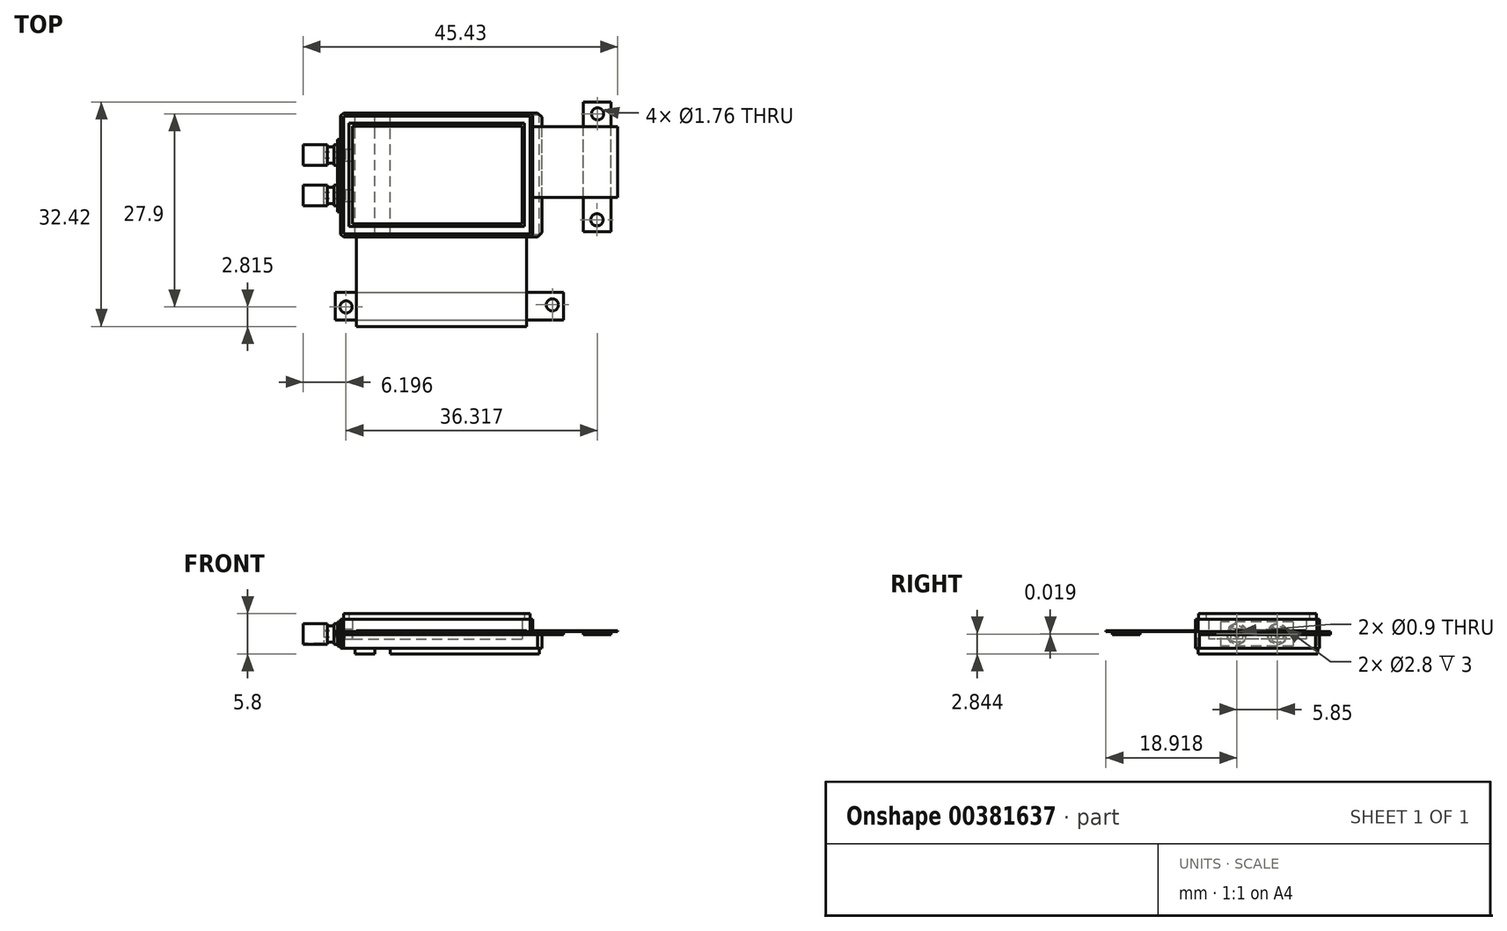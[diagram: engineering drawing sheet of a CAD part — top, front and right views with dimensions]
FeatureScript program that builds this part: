
annotation { "Feature Type Name" : "Feature", "Feature Type Description" : "" }
export const myFeature = defineFeature(function(context is Context, id is Id, definition is map)
    precondition{}
    {
        {
            var Q0;
            Q0=qCreatedBy(makeId("Top.planeOp"),FACE);
            var sketch = newSketch(context, id + "F0", { "sketchPlane" : qUnion([Q0])});
            skLineSegment(sketch, "E0.bottom", {"start": v(-8, 13.05) * mm, "end": v(19.71, 13.05) * mm});
            skLineSegment(sketch, "E0.top", {"start": v(-8, -4.87) * mm, "end": v(19.71, -4.87) * mm});
            skLineSegment(sketch, "E0.left", {"start": v(-8, 13.05) * mm, "end": v(-8, -4.87) * mm});
            skLineSegment(sketch, "E0.right", {"start": v(19.71, 13.05) * mm, "end": v(19.71, -4.87) * mm});
            skLineSegment(sketch, "E1.bottom", {"start": v(-6.33, 11.15) * mm, "end": v(18.21, 11.15) * mm});
            skLineSegment(sketch, "E1.top", {"start": v(-6.33, -2.97) * mm, "end": v(18.21, -2.97) * mm});
            skLineSegment(sketch, "E1.left", {"start": v(-6.33, 11.15) * mm, "end": v(-6.33, -2.97) * mm});
            skLineSegment(sketch, "E1.right", {"start": v(18.21, 11.15) * mm, "end": v(18.21, -2.97) * mm});
            skSolve(sketch);
        }
        {
            var Q0;
            Q0=makeQuery(id+"F0.imprint","IMPRINT",FACE,{"disambiguationData":[TD([[makeQuery(id+"F0.imprint","IMPRINT",EDGE,{"derivedFrom":sQuery(id+"F0.wireOp",EDGE,"E0.bottom")}),-1.0]])]});
            extrude(context, id + "F1", {"entities" : qUnion([Q0]), "depth" : 1.78 * mm});
        }
        {
            var Q0;
            Q0=makeQuery(id+"F1.opExtrude","CAP_FACE",FACE,{"disambiguationData":[OSD([sQuery(id+"F0.wireOp",EDGE,"E0.bottom"),sQuery(id+"F0.wireOp",EDGE,"E0.top"),sQuery(id+"F0.wireOp",EDGE,"E0.left"),sQuery(id+"F0.wireOp",EDGE,"E0.right"),sQuery(id+"F0.wireOp",EDGE,"E1.bottom"),sQuery(id+"F0.wireOp",EDGE,"E1.top"),sQuery(id+"F0.wireOp",EDGE,"E1.left"),sQuery(id+"F0.wireOp",EDGE,"E1.right")])],"isStart":false});
            var sketch = newSketch(context, id + "F2", { "sketchPlane" : qUnion([Q0])});
            skLineSegment(sketch, "E2.bottom", {"start": v(-7.6, 12.6) * mm, "end": v(19.32, 12.6) * mm});
            skLineSegment(sketch, "E2.top", {"start": v(-7.6, -4.41) * mm, "end": v(19.32, -4.41) * mm});
            skLineSegment(sketch, "E2.left", {"start": v(-7.6, 12.6) * mm, "end": v(-7.6, -4.41) * mm});
            skLineSegment(sketch, "E2.right", {"start": v(19.32, 12.6) * mm, "end": v(19.32, -4.41) * mm});
            skLineSegment(sketch, "E3.bottom", {"start": v(-6.79, 11.56) * mm, "end": v(18.51, 11.56) * mm});
            skLineSegment(sketch, "E3.top", {"start": v(-6.79, -3.34) * mm, "end": v(18.51, -3.34) * mm});
            skLineSegment(sketch, "E3.left", {"start": v(-6.79, 11.56) * mm, "end": v(-6.79, -3.34) * mm});
            skLineSegment(sketch, "E3.right", {"start": v(18.51, 11.56) * mm, "end": v(18.51, -3.34) * mm});
            skSolve(sketch);
        }
        {
            var Q0;
            Q0=makeQuery(id+"F2.imprint","IMPRINT",FACE,{"disambiguationData":[TD([[makeQuery(id+"F2.imprint","IMPRINT",EDGE,{"derivedFrom":sQuery(id+"F2.wireOp",EDGE,"E2.bottom")}),-1.0]])]});
            extrude(context, id + "F3", {"entities" : qUnion([Q0]), "operationType" : NewBodyOperationType.ADD, "depth" : 0.8 * mm});
        }
        {
            var Q0;
            Q0=makeQuery(id+"F1.opExtrude","CAP_FACE",FACE,{"disambiguationData":[OSD([sQuery(id+"F0.wireOp",EDGE,"E0.bottom"),sQuery(id+"F0.wireOp",EDGE,"E0.top"),sQuery(id+"F0.wireOp",EDGE,"E0.left"),sQuery(id+"F0.wireOp",EDGE,"E0.right"),sQuery(id+"F0.wireOp",EDGE,"E1.bottom"),sQuery(id+"F0.wireOp",EDGE,"E1.top"),sQuery(id+"F0.wireOp",EDGE,"E1.left"),sQuery(id+"F0.wireOp",EDGE,"E1.right")])],"isStart":true});
            var sketch = newSketch(context, id + "F4", { "sketchPlane" : qUnion([Q0])});
            skLineSegment(sketch, "E4.bottom", {"start": v(-8, 4.87) * mm, "end": v(21.03, 4.87) * mm});
            skLineSegment(sketch, "E4.top", {"start": v(-8, -13.05) * mm, "end": v(21.03, -13.05) * mm});
            skLineSegment(sketch, "E4.left", {"start": v(-8, 4.87) * mm, "end": v(-8, -13.05) * mm});
            skLineSegment(sketch, "E4.right", {"start": v(21.03, 4.87) * mm, "end": v(21.03, -13.05) * mm});
            skSolve(sketch);
        }
        {
            var Q0;
            Q0 = qSketchRegion(id + "F4", true);
            var Q1;
            Q1=makeQuery(id+"F4.imprint","IMPRINT",FACE,{"disambiguationData":[TD([[makeQuery(id+"F4.imprint","IMPRINT",EDGE,{"derivedFrom":makeQuery(id+"F1.opExtrude","CAP_EDGE",EDGE,{"disambiguationData":[OSD([sQuery(id+"F0.wireOp",EDGE,"E1.bottom")])],"isStart":true})}),1.0]])]});
            var Q2;
            {var subQ1=sQuery(id+"F4.wireOp",EDGE,"E4.left");Q2=makeQuery(id+"F4.imprint","IMPRINT",FACE,{"disambiguationData":[TD([[makeQuery(id+"F4.imprint","IMPRINT",EDGE,{"derivedFrom":subQ1}),-1.0]])]});}
            extrude(context, id + "F5", {"entities" : qUnion([Q0, Q1, Q2]), "operationType" : NewBodyOperationType.ADD, "depth" : 2.42 * mm});
        }
        {
            var Q0;
            Q0=makeQuery(id+"F5.opExtrude","CAP_FACE",FACE,{"disambiguationData":[OSD([sQuery(id+"F4.wireOp",EDGE,"E4.bottom"),sQuery(id+"F4.wireOp",EDGE,"E4.top"),sQuery(id+"F4.wireOp",EDGE,"E4.left"),sQuery(id+"F4.wireOp",EDGE,"E4.right")])],"isStart":false});
            var sketch = newSketch(context, id + "F6", { "sketchPlane" : qUnion([Q0])});
            skLineSegment(sketch, "E5.bottom", {"start": v(-0.85, 4.49) * mm, "end": v(20.66, 4.49) * mm});
            skLineSegment(sketch, "E5.top", {"start": v(-0.85, -12.76) * mm, "end": v(20.66, -12.76) * mm});
            skLineSegment(sketch, "E5.left", {"start": v(-0.85, 4.49) * mm, "end": v(-0.85, -12.76) * mm});
            skLineSegment(sketch, "E5.right", {"start": v(20.66, 4.49) * mm, "end": v(20.66, -12.76) * mm});
            skSolve(sketch);
        }
        {
            var Q0;
            Q0=makeQuery(id+"F6.imprint","IMPRINT",FACE,{"disambiguationData":[TD([[makeQuery(id+"F6.imprint","IMPRINT",EDGE,{"derivedFrom":sQuery(id+"F6.wireOp",EDGE,"E5.bottom")}),-1.0]])]});
            extrude(context, id + "F7", {"entities" : qUnion([Q0]), "operationType" : NewBodyOperationType.ADD, "depth" : 0.8 * mm});
        }
        {
            var Q0;
            Q0=makeQuery(id+"F5.opExtrude","CAP_FACE",FACE,{"disambiguationData":[OSD([sQuery(id+"F4.wireOp",EDGE,"E4.bottom"),sQuery(id+"F4.wireOp",EDGE,"E4.top"),sQuery(id+"F4.wireOp",EDGE,"E4.left"),sQuery(id+"F4.wireOp",EDGE,"E4.right")])],"isStart":false});
            var sketch = newSketch(context, id + "F8", { "sketchPlane" : qUnion([Q0])});
            skLineSegment(sketch, "E6.bottom", {"start": v(-5.95, 4.44) * mm, "end": v(-3.08, 4.44) * mm});
            skLineSegment(sketch, "E6.top", {"start": v(-5.95, -12.64) * mm, "end": v(-3.08, -12.64) * mm});
            skLineSegment(sketch, "E6.left", {"start": v(-5.95, 4.44) * mm, "end": v(-5.95, -12.64) * mm});
            skLineSegment(sketch, "E6.right", {"start": v(-3.08, 4.44) * mm, "end": v(-3.08, -12.64) * mm});
            skSolve(sketch);
        }
        {
            var Q0;
            Q0=makeQuery(id+"F8.imprint","IMPRINT",FACE,{"disambiguationData":[TD([[makeQuery(id+"F8.imprint","IMPRINT",EDGE,{"derivedFrom":sQuery(id+"F8.wireOp",EDGE,"E6.bottom")}),-1.0]])]});
            extrude(context, id + "F9", {"entities" : qUnion([Q0]), "operationType" : NewBodyOperationType.ADD, "depth" : 0.8 * mm});
        }
        {
            var Q0;
            Q0=makeQuery(id+"F5.boolean.opBoolean","MERGE",FACE,{"derivedFrom":[makeQuery(id+"F1.opExtrude","SWEPT_FACE",FACE,{"disambiguationData":[OSD([sQuery(id+"F0.wireOp",EDGE,"E0.left")])]}),makeQuery(id+"F5.opExtrude","SWEPT_FACE",FACE,{"disambiguationData":[OSD([sQuery(id+"F4.wireOp",EDGE,"E4.left")])]})]});
            var sketch = newSketch(context, id + "F10", { "sketchPlane" : qUnion([Q0])});
            skLineSegment(sketch, "E7.bottom", {"start": v(-9.23, 1.39) * mm, "end": v(1.27, 1.39) * mm});
            skLineSegment(sketch, "E7.top", {"start": v(-9.23, -2.1) * mm, "end": v(1.27, -2.1) * mm});
            skLineSegment(sketch, "E7.left", {"start": v(-9.23, 1.39) * mm, "end": v(-9.23, -2.1) * mm});
            skLineSegment(sketch, "E7.right", {"start": v(1.27, 1.39) * mm, "end": v(1.27, -2.1) * mm});
            skSolve(sketch);
        }
        {
            var Q0;
            Q0=makeQuery(id+"F10.imprint","IMPRINT",FACE,{"disambiguationData":[TD([[makeQuery(id+"F10.imprint","IMPRINT",EDGE,{"derivedFrom":sQuery(id+"F10.wireOp",EDGE,"E7.bottom")}),-1.0]])]});
            extrude(context, id + "F11", {"entities" : qUnion([Q0]), "operationType" : NewBodyOperationType.ADD, "depth" : 0.5 * mm});
        }
        {
            var Q0;
            Q0=makeQuery(id+"F11.opExtrude","CAP_FACE",FACE,{"disambiguationData":[OSD([sQuery(id+"F10.wireOp",EDGE,"E7.bottom"),sQuery(id+"F10.wireOp",EDGE,"E7.top"),sQuery(id+"F10.wireOp",EDGE,"E7.left"),sQuery(id+"F10.wireOp",EDGE,"E7.right")])],"isStart":false});
            var sketch = newSketch(context, id + "F12", { "sketchPlane" : qUnion([Q0])});
            skCircle(sketch, "E8", {"center": v(-6.96, -0.38) * mm, "radius": 1.5 * mm});
            skCircle(sketch, "E9", {"center": v(-1.1, -0.36) * mm, "radius": 1.5 * mm});
            skSolve(sketch);
        }
        {
            var Q0;
            Q0=makeQuery(id+"F12.imprint","IMPRINT",FACE,{"disambiguationData":[TD([[makeQuery(id+"F12.imprint","IMPRINT",EDGE,{"derivedFrom":sQuery(id+"F12.wireOp",EDGE,"E8")}),1.0]])]});
            var Q1;
            Q1=makeQuery(id+"F12.imprint","IMPRINT",FACE,{"disambiguationData":[TD([[makeQuery(id+"F12.imprint","IMPRINT",EDGE,{"derivedFrom":sQuery(id+"F12.wireOp",EDGE,"E9")}),1.0]])]});
            extrude(context, id + "F13", {"entities" : qUnion([Q0, Q1]), "operationType" : NewBodyOperationType.ADD, "depth" : 0.5 * mm});
        }
        {
            var Q0;
            Q0=makeQuery(id+"F13.opExtrude","CAP_FACE",FACE,{"disambiguationData":[OSD([sQuery(id+"F12.wireOp",EDGE,"E8")])],"isStart":false});
            var sketch = newSketch(context, id + "F14", { "sketchPlane" : qUnion([Q0])});
            skCircle(sketch, "E10", {"center": v(-6.96, -0.38) * mm, "radius": 1.17 * mm});
            skSolve(sketch);
        }
        {
            var Q0;
            Q0=makeQuery(id+"F14.imprint","IMPRINT",FACE,{"disambiguationData":[TD([[makeQuery(id+"F14.imprint","IMPRINT",EDGE,{"derivedFrom":sQuery(id+"F14.wireOp",EDGE,"E10")}),1.0]])]});
            extrude(context, id + "F15", {"entities" : qUnion([Q0]), "operationType" : NewBodyOperationType.ADD, "depth" : 0.95 * mm});
        }
        {
            var Q0;
            Q0=makeQuery(id+"F13.opExtrude","CAP_FACE",FACE,{"disambiguationData":[OSD([sQuery(id+"F12.wireOp",EDGE,"E9")])],"isStart":false});
            var sketch = newSketch(context, id + "F16", { "sketchPlane" : qUnion([Q0])});
            skCircle(sketch, "E11", {"center": v(-1.1, -0.36) * mm, "radius": 1.17 * mm});
            skSolve(sketch);
        }
        {
            var Q0;
            Q0=makeQuery(id+"F16.imprint","IMPRINT",FACE,{"disambiguationData":[TD([[makeQuery(id+"F16.imprint","IMPRINT",EDGE,{"derivedFrom":sQuery(id+"F16.wireOp",EDGE,"E11")}),1.0]])]});
            extrude(context, id + "F17", {"entities" : qUnion([Q0]), "operationType" : NewBodyOperationType.ADD, "depth" : 0.95 * mm});
        }
        {
            var Q0;
            Q0=makeQuery(id+"F15.opExtrude","CAP_FACE",FACE,{"disambiguationData":[OSD([sQuery(id+"F14.wireOp",EDGE,"E10")])],"isStart":false});
            var sketch = newSketch(context, id + "F18", { "sketchPlane" : qUnion([Q0])});
            skCircle(sketch, "E12", {"center": v(-6.96, -0.38) * mm, "radius": 1.5 * mm});
            skSolve(sketch);
        }
        {
            var Q0;
            Q0=makeQuery(id+"F18.imprint","IMPRINT",FACE,{"disambiguationData":[TD([[makeQuery(id+"F18.imprint","IMPRINT",EDGE,{"derivedFrom":sQuery(id+"F18.wireOp",EDGE,"E12")}),1.0]])]});
            var Q1;
            Q1=makeQuery(id+"F18.imprint","IMPRINT",FACE,{"disambiguationData":[TD([[makeQuery(id+"F18.imprint","IMPRINT",EDGE,{"derivedFrom":makeQuery(id+"F15.opExtrude","CAP_EDGE",EDGE,{"disambiguationData":[OSD([sQuery(id+"F14.wireOp",EDGE,"E10")])],"isStart":false})}),1.0]])]});
            extrude(context, id + "F19", {"entities" : qUnion([Q0, Q1]), "operationType" : NewBodyOperationType.ADD, "depth" : 3.48 * mm});
        }
        {
            var Q0;
            Q0=makeQuery(id+"F17.opExtrude","CAP_FACE",FACE,{"disambiguationData":[OSD([sQuery(id+"F16.wireOp",EDGE,"E11")])],"isStart":false});
            var sketch = newSketch(context, id + "F20", { "sketchPlane" : qUnion([Q0])});
            skCircle(sketch, "E13", {"center": v(-1.1, -0.36) * mm, "radius": 1.5 * mm});
            skSolve(sketch);
        }
        {
            var Q0;
            Q0=makeQuery(id+"F20.imprint","IMPRINT",FACE,{"disambiguationData":[TD([[makeQuery(id+"F20.imprint","IMPRINT",EDGE,{"derivedFrom":makeQuery(id+"F17.opExtrude","CAP_EDGE",EDGE,{"disambiguationData":[OSD([sQuery(id+"F16.wireOp",EDGE,"E11")])],"isStart":false})}),1.0]])]});
            var Q1;
            Q1=makeQuery(id+"F20.imprint","IMPRINT",FACE,{"disambiguationData":[TD([[makeQuery(id+"F20.imprint","IMPRINT",EDGE,{"derivedFrom":sQuery(id+"F20.wireOp",EDGE,"E13")}),1.0]])]});
            extrude(context, id + "F21", {"entities" : qUnion([Q0, Q1]), "operationType" : NewBodyOperationType.ADD, "depth" : 3.48 * mm});
        }
        {
            var Q0;
            Q0=makeQuery(id+"F5.boolean.opBoolean","MERGE",FACE,{"derivedFrom":[makeQuery(id+"F1.opExtrude","SWEPT_FACE",FACE,{"disambiguationData":[OSD([sQuery(id+"F0.wireOp",EDGE,"E0.top")])]}),makeQuery(id+"F5.opExtrude","SWEPT_FACE",FACE,{"disambiguationData":[OSD([sQuery(id+"F4.wireOp",EDGE,"E4.bottom")])]})]});
            var sketch = newSketch(context, id + "F22", { "sketchPlane" : qUnion([Q0])});
            skLineSegment(sketch, "E14.bottom", {"start": v(-5.74, 0) * mm, "end": v(18.82, 0) * mm});
            skLineSegment(sketch, "E14.top", {"start": v(-5.74, 0.14) * mm, "end": v(18.82, 0.14) * mm});
            skLineSegment(sketch, "E14.left", {"start": v(-5.74, 0.14) * mm, "end": v(-5.74, 0) * mm});
            skLineSegment(sketch, "E14.right", {"start": v(18.82, 0.14) * mm, "end": v(18.82, 0) * mm});
            skSolve(sketch);
        }
        {
            var Q0;
            Q0=makeQuery(id+"F22.imprint","IMPRINT",FACE,{"disambiguationData":[TD([[makeQuery(id+"F22.imprint","IMPRINT",EDGE,{"derivedFrom":sQuery(id+"F22.wireOp",EDGE,"E14.bottom")}),1.0]])]});
            extrude(context, id + "F23", {"entities" : qUnion([Q0]), "operationType" : NewBodyOperationType.ADD, "depth" : 12.94 * mm});
        }
        {
            var Q0;
            Q0=makeQuery(id+"F23.opExtrude","SWEPT_FACE",FACE,{"disambiguationData":[OSD([sQuery(id+"F22.wireOp",EDGE,"E14.bottom")])]});
            var sketch = newSketch(context, id + "F24", { "sketchPlane" : qUnion([Q0])});
            skLineSegment(sketch, "E15.top", {"start": v(-8.82, 12.87) * mm, "end": v(24.16, 12.87) * mm});
            skLineSegment(sketch, "E15.left", {"start": v(-8.82, 17.81) * mm, "end": v(-8.82, 12.87) * mm});
            skLineSegment(sketch, "E15.right", {"start": v(24.16, 18.6) * mm, "end": v(24.16, 12.87) * mm});
            skCircle(sketch, "E16", {"center": v(-7.23, 15) * mm, "radius": 0.88 * mm});
            skCircle(sketch, "E17", {"center": v(22.56, 14.68) * mm, "radius": 0.88 * mm});
            skLineSegment(sketch, "E18", {"start": v(-8.82, 16.87) * mm, "end": v(24.16, 16.87) * mm});
            skSolve(sketch);
        }
        {
            var Q0;
            Q0=makeQuery(id+"F24.imprint","IMPRINT",FACE,{"disambiguationData":[TD([[makeQuery(id+"F24.imprint","IMPRINT",EDGE,{"derivedFrom":sQuery(id+"F24.wireOp",EDGE,"E17")}),-1.0]])]});
            var Q1;
            {var subQ0=sQuery(id+"F24.wireOp",EDGE,"E15.top");var subQ1=sQuery(id+"F22.wireOp",EDGE,"E14.bottom");var subQ2=makeQuery(id+"F23.opExtrude","SWEPT_EDGE",EDGE,{"disambiguationData":[OSD([subQ1,sQuery(id+"F22.wireOp",EDGE,"E14.left")])]});var subQ3=makeQuery(id+"F24.imprint","INTERSECT",VERTEX,{"derivedFrom":[subQ2,subQ0]});Q1=makeQuery(id+"F24.imprint","IMPRINT",FACE,{"disambiguationData":[TD([[makeQuery(id+"F24.imprint","IMPRINT",EDGE,{"disambiguationData":[TD([[subQ3,-1.0]])],"derivedFrom":subQ0}),1.0]])]});}
            var Q2;
            Q2=makeQuery(id+"F24.imprint","IMPRINT",FACE,{"disambiguationData":[TD([[makeQuery(id+"F24.imprint","IMPRINT",EDGE,{"derivedFrom":sQuery(id+"F24.wireOp",EDGE,"E16")}),-1.0]])]});
            extrude(context, id + "F25", {"entities" : qUnion([Q0, Q1, Q2]), "operationType" : NewBodyOperationType.ADD, "depth" : 0.47 * mm});
        }
        {
            var Q0;
            Q0=makeQuery(id+"F1.opExtrude","SWEPT_FACE",FACE,{"disambiguationData":[OSD([sQuery(id+"F0.wireOp",EDGE,"E0.right")])]});
            var sketch = newSketch(context, id + "F26", { "sketchPlane" : qUnion([Q0])});
            skLineSegment(sketch, "E19.bottom", {"start": v(0.83, 0) * mm, "end": v(11.09, 0) * mm});
            skLineSegment(sketch, "E19.top", {"start": v(0.83, 0.12) * mm, "end": v(11.09, 0.12) * mm});
            skLineSegment(sketch, "E19.left", {"start": v(0.83, 0) * mm, "end": v(0.83, 0.12) * mm});
            skLineSegment(sketch, "E19.right", {"start": v(11.09, 0) * mm, "end": v(11.09, 0.12) * mm});
            skSolve(sketch);
        }
        {
            var Q0;
            Q0=makeQuery(id+"F26.imprint","IMPRINT",FACE,{"disambiguationData":[TD([[makeQuery(id+"F26.imprint","IMPRINT",EDGE,{"derivedFrom":sQuery(id+"F26.wireOp",EDGE,"E19.bottom")}),-1.0]])]});
            extrude(context, id + "F27", {"entities" : qUnion([Q0]), "operationType" : NewBodyOperationType.ADD, "depth" : 12.29 * mm});
        }
        {
            var Q0;
            Q0=makeQuery(id+"F27.opExtrude","SWEPT_FACE",FACE,{"disambiguationData":[OSD([sQuery(id+"F26.wireOp",EDGE,"E19.bottom")])]});
            var sketch = newSketch(context, id + "F28", { "sketchPlane" : qUnion([Q0])});
            skLineSegment(sketch, "E20.bottom", {"start": v(27.03, 4.1) * mm, "end": v(31.03, 4.1) * mm});
            skLineSegment(sketch, "E20.top", {"start": v(27.03, -14.6) * mm, "end": v(31.03, -14.6) * mm});
            skLineSegment(sketch, "E20.left", {"start": v(27.03, 4.1) * mm, "end": v(27.03, -14.6) * mm});
            skLineSegment(sketch, "E20.right", {"start": v(31.03, 4.1) * mm, "end": v(31.03, -14.6) * mm});
            skCircle(sketch, "E21", {"center": v(29, 2.4) * mm, "radius": 0.88 * mm});
            skCircle(sketch, "E22", {"center": v(29.08, -12.9) * mm, "radius": 0.88 * mm});
            skSolve(sketch);
        }
        {
            var Q0;
            {var subQ1=sQuery(id+"F28.wireOp",EDGE,"E20.bottom");Q0=makeQuery(id+"F28.imprint","IMPRINT",FACE,{"disambiguationData":[TD([[makeQuery(id+"F28.imprint","IMPRINT",EDGE,{"derivedFrom":subQ1}),-1.0]])]});}
            var Q1;
            {var subQ0=sQuery(id+"F28.wireOp",EDGE,"E20.left");var subQ1=sQuery(id+"F26.wireOp",EDGE,"E19.bottom");var subQ2=makeQuery(id+"F27.opExtrude","SWEPT_FACE",FACE,{"disambiguationData":[OSD([subQ1])]});var subQ3=sQuery(id+"F26.wireOp",EDGE,"E19.left");var subQ4=sQuery(id+"F0.wireOp",EDGE,"E0.right");var subQ5=makeQuery(id+"F27.boolean.opBoolean","SPLIT",EDGE,{"disambiguationData":[topologyDisambiguationEdgeConnected([subQ2])],"derivedFrom":makeQuery(id+"F27.opExtrude","SWEPT_EDGE",EDGE,{"disambiguationData":[OSD([subQ4,subQ1,subQ3])]})});var subQ6=makeQuery(id+"F28.imprint","INTERSECT",VERTEX,{"derivedFrom":[subQ5,subQ0]});Q1=makeQuery(id+"F28.imprint","IMPRINT",FACE,{"disambiguationData":[TD([[makeQuery(id+"F28.imprint","IMPRINT",EDGE,{"disambiguationData":[TD([[subQ6,-1.0]])],"derivedFrom":subQ0}),1.0]])]});}
            var Q2;
            {var subQ1=sQuery(id+"F28.wireOp",EDGE,"E20.top");Q2=makeQuery(id+"F28.imprint","IMPRINT",FACE,{"disambiguationData":[TD([[makeQuery(id+"F28.imprint","IMPRINT",EDGE,{"derivedFrom":subQ1}),1.0]])]});}
            extrude(context, id + "F29", {"entities" : qUnion([Q0, Q1, Q2]), "operationType" : NewBodyOperationType.ADD, "depth" : 0.47 * mm});
        }
        {
            var Q0;
            Q0=makeQuery(id+"F19.opExtrude","CAP_FACE",FACE,{"disambiguationData":[OSD([sQuery(id+"F18.wireOp",EDGE,"E12")])],"isStart":false});
            var sketch = newSketch(context, id + "F30", { "sketchPlane" : qUnion([Q0])});
            skCircle(sketch, "E23", {"center": v(-6.96, -0.38) * mm, "radius": 1.4 * mm});
            skSolve(sketch);
        }
        {
            var Q0;
            Q0=makeQuery(id+"F21.opExtrude","CAP_FACE",FACE,{"disambiguationData":[OSD([sQuery(id+"F20.wireOp",EDGE,"E13")])],"isStart":false});
            var sketch = newSketch(context, id + "F31", { "sketchPlane" : qUnion([Q0])});
            skCircle(sketch, "E24", {"center": v(-1.1, -0.36) * mm, "radius": 1.4 * mm});
            skSolve(sketch);
        }
        {
            var Q0;
            Q0=makeQuery(id+"F30.imprint","IMPRINT",FACE,{"disambiguationData":[TD([[makeQuery(id+"F30.imprint","IMPRINT",EDGE,{"derivedFrom":sQuery(id+"F30.wireOp",EDGE,"E23")}),1.0]])]});
            extrude(context, id + "F32", {"entities" : qUnion([Q0]), "operationType" : NewBodyOperationType.REMOVE, "oppositeDirection" : true, "depth" : 3 * mm});
        }
        {
            var Q0;
            Q0=makeQuery(id+"F31.imprint","IMPRINT",FACE,{"disambiguationData":[TD([[makeQuery(id+"F31.imprint","IMPRINT",EDGE,{"derivedFrom":sQuery(id+"F31.wireOp",EDGE,"E24")}),1.0]])]});
            extrude(context, id + "F33", {"entities" : qUnion([Q0]), "operationType" : NewBodyOperationType.REMOVE, "oppositeDirection" : true, "depth" : 3 * mm});
        }
        {
            var Q0;
            Q0=makeQuery(id+"F32.boolean.opBoolean","COPY",FACE,{"derivedFrom":makeQuery(id+"F32.opExtrude","CAP_FACE",FACE,{"disambiguationData":[OSD([sQuery(id+"F30.wireOp",EDGE,"E23")])],"isStart":false})});
            var sketch = newSketch(context, id + "F34", { "sketchPlane" : qUnion([Q0])});
            skCircle(sketch, "E25", {"center": v(-6.96, -0.38) * mm, "radius": 0.45 * mm});
            skSolve(sketch);
        }
        {
            var Q0;
            Q0=makeQuery(id+"F33.boolean.opBoolean","COPY",FACE,{"derivedFrom":makeQuery(id+"F33.opExtrude","CAP_FACE",FACE,{"disambiguationData":[OSD([sQuery(id+"F31.wireOp",EDGE,"E24")])],"isStart":false})});
            var sketch = newSketch(context, id + "F35", { "sketchPlane" : qUnion([Q0])});
            skCircle(sketch, "E26", {"center": v(-1.1, -0.36) * mm, "radius": 0.45 * mm});
            skSolve(sketch);
        }
        {
            var Q0;
            Q0=makeQuery(id+"F4.imprint","IMPRINT",FACE,{"disambiguationData":[TD([[makeQuery(id+"F4.imprint","IMPRINT",EDGE,{"derivedFrom":makeQuery(id+"F1.opExtrude","CAP_EDGE",EDGE,{"disambiguationData":[OSD([sQuery(id+"F0.wireOp",EDGE,"E1.bottom")])],"isStart":true})}),1.0]])]});
            extrude(context, id + "F36", {"entities" : qUnion([Q0]), "operationType" : NewBodyOperationType.REMOVE, "oppositeDirection" : true, "depth" : 0.5 * mm});
        }
        {
            var Q0;
            Q0=makeQuery(id+"F34.imprint","IMPRINT",FACE,{"disambiguationData":[TD([[makeQuery(id+"F34.imprint","IMPRINT",EDGE,{"derivedFrom":sQuery(id+"F34.wireOp",EDGE,"E25")}),1.0]])]});
            extrude(context, id + "F37", {"entities" : qUnion([Q0]), "operationType" : NewBodyOperationType.REMOVE, "oppositeDirection" : true, "depth" : 5 * mm});
        }
        {
            var Q0;
            Q0=makeQuery(id+"F4.imprint","IMPRINT",FACE,{"disambiguationData":[TD([[makeQuery(id+"F4.imprint","IMPRINT",EDGE,{"derivedFrom":makeQuery(id+"F1.opExtrude","CAP_EDGE",EDGE,{"disambiguationData":[OSD([sQuery(id+"F0.wireOp",EDGE,"E1.bottom")])],"isStart":true})}),1.0]])]});
            extrude(context, id + "F38", {"entities" : qUnion([Q0]), "operationType" : NewBodyOperationType.REMOVE, "depth" : 1.1 * mm});
        }
        {
            var Q0;
            Q0=makeQuery(id+"F35.imprint","IMPRINT",FACE,{"disambiguationData":[TD([[makeQuery(id+"F35.imprint","IMPRINT",EDGE,{"derivedFrom":sQuery(id+"F35.wireOp",EDGE,"E26")}),1.0]])]});
            extrude(context, id + "F39", {"entities" : qUnion([Q0]), "operationType" : NewBodyOperationType.REMOVE, "oppositeDirection" : true, "depth" : 5 * mm});
        }
        {
            var Q0;
            {var subQ0=sQuery(id+"F0.wireOp",EDGE,"E1.left");Q0=makeQuery(id+"F38.boolean.opBoolean","MERGE",FACE,{"derivedFrom":[makeQuery(id+"F1.opExtrude","SWEPT_FACE",FACE,{"disambiguationData":[OSD([subQ0])]}),makeQuery(id+"F38.opExtrude","SWEPT_FACE",FACE,{"disambiguationData":[OSD([subQ0])]})]});}
            var sketch = newSketch(context, id + "F40", { "sketchPlane" : qUnion([Q0])});
            skLineSegment(sketch, "E27.bottom", {"start": v(1.96, -1.1) * mm, "end": v(0.26, -1.1) * mm});
            skLineSegment(sketch, "E27.top", {"start": v(1.96, 0.39) * mm, "end": v(0.26, 0.39) * mm});
            skLineSegment(sketch, "E27.left", {"start": v(1.96, -1.1) * mm, "end": v(1.96, 0.39) * mm});
            skLineSegment(sketch, "E27.right", {"start": v(0.26, -1.1) * mm, "end": v(0.26, 0.39) * mm});
            skPoint(sketch, "E27.middle", {"position": v(1.1, -0.36) * mm});
            skLineSegment(sketch, "E28.bottom", {"start": v(7.8, -1.1) * mm, "end": v(6.1, -1.1) * mm});
            skLineSegment(sketch, "E28.top", {"start": v(7.8, 0.35) * mm, "end": v(6.1, 0.35) * mm});
            skLineSegment(sketch, "E28.left", {"start": v(7.8, -1.1) * mm, "end": v(7.8, 0.35) * mm});
            skLineSegment(sketch, "E28.right", {"start": v(6.1, -1.1) * mm, "end": v(6.1, 0.35) * mm});
            skPoint(sketch, "E28.middle", {"position": v(6.96, -0.38) * mm});
            skSolve(sketch);
        }
        {
            var Q0;
            Q0=makeQuery(id+"F40.imprint","IMPRINT",FACE,{"disambiguationData":[TD([[makeQuery(id+"F40.imprint","IMPRINT",EDGE,{"derivedFrom":sQuery(id+"F40.wireOp",EDGE,"E27.bottom")}),-1.0]])]});
            var Q1;
            Q1=makeQuery(id+"F40.imprint","IMPRINT",FACE,{"disambiguationData":[TD([[makeQuery(id+"F40.imprint","IMPRINT",EDGE,{"derivedFrom":sQuery(id+"F40.wireOp",EDGE,"E28.bottom")}),-1.0]])]});
            extrude(context, id + "F41", {"entities" : qUnion([Q0, Q1]), "operationType" : NewBodyOperationType.REMOVE, "oppositeDirection" : true, "depth" : 1 * mm});
        }
        {
            var Q0;
            Q0=makeQuery(id+"F5.boolean.opBoolean","MERGE",EDGE,{"derivedFrom":[makeQuery(id+"F1.opExtrude","SWEPT_EDGE",EDGE,{"disambiguationData":[OSD([sQuery(id+"F0.wireOp",EDGE,"E0.bottom"),sQuery(id+"F0.wireOp",EDGE,"E0.left")])]}),makeQuery(id+"F5.opExtrude","SWEPT_EDGE",EDGE,{"disambiguationData":[OSD([sQuery(id+"F4.wireOp",EDGE,"E4.top"),sQuery(id+"F4.wireOp",EDGE,"E4.left")])]})]});
            chamfer(context, id + "F42", {"entities" : qUnion([Q0]), "width" : 0.4 * mm, "tangentPropagation" : true});
        }
        {
            var Q0;
            Q0=makeQuery(id+"F5.boolean.opBoolean","MERGE",EDGE,{"derivedFrom":[makeQuery(id+"F1.opExtrude","SWEPT_EDGE",EDGE,{"disambiguationData":[OSD([sQuery(id+"F0.wireOp",EDGE,"E0.top"),sQuery(id+"F0.wireOp",EDGE,"E0.left")])]}),makeQuery(id+"F5.opExtrude","SWEPT_EDGE",EDGE,{"disambiguationData":[OSD([sQuery(id+"F4.wireOp",EDGE,"E4.bottom"),sQuery(id+"F4.wireOp",EDGE,"E4.left")])]})]});
            chamfer(context, id + "F43", {"entities" : qUnion([Q0]), "width" : 0.4 * mm, "tangentPropagation" : true});
        }
        {
            var Q0;
            Q0=makeQuery(id+"F1.opExtrude","SWEPT_EDGE",EDGE,{"disambiguationData":[OSD([sQuery(id+"F0.wireOp",EDGE,"E0.bottom"),sQuery(id+"F0.wireOp",EDGE,"E0.right")])]});
            chamfer(context, id + "F44", {"entities" : qUnion([Q0]), "width" : 0.4 * mm, "tangentPropagation" : true});
        }
        {
            var Q0;
            Q0=makeQuery(id+"F1.opExtrude","SWEPT_EDGE",EDGE,{"disambiguationData":[OSD([sQuery(id+"F0.wireOp",EDGE,"E0.top"),sQuery(id+"F0.wireOp",EDGE,"E0.right")])]});
            chamfer(context, id + "F45", {"entities" : qUnion([Q0]), "width" : 0.4 * mm, "tangentPropagation" : true});
        }
        {
            var Q0;
            Q0=makeQuery(id+"F5.opExtrude","SWEPT_EDGE",EDGE,{"disambiguationData":[OSD([sQuery(id+"F4.wireOp",EDGE,"E4.bottom"),sQuery(id+"F4.wireOp",EDGE,"E4.right")])]});
            chamfer(context, id + "F46", {"entities" : qUnion([Q0]), "width" : 0.6 * mm, "tangentPropagation" : true});
        }
        {
            var Q0;
            Q0=makeQuery(id+"F5.opExtrude","SWEPT_EDGE",EDGE,{"disambiguationData":[OSD([sQuery(id+"F4.wireOp",EDGE,"E4.top"),sQuery(id+"F4.wireOp",EDGE,"E4.right")])]});
            chamfer(context, id + "F47", {"entities" : qUnion([Q0]), "width" : 0.6 * mm, "tangentPropagation" : true});
        }
    });
